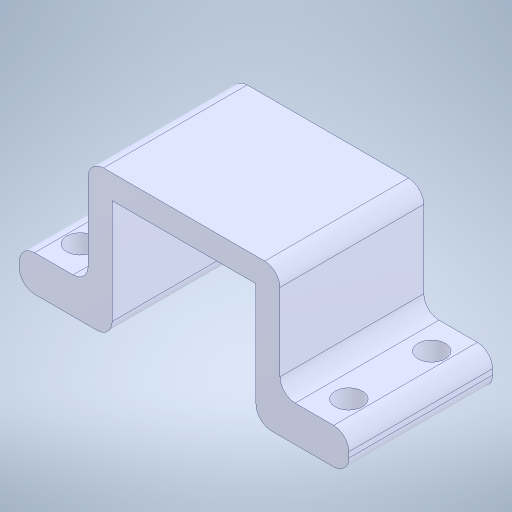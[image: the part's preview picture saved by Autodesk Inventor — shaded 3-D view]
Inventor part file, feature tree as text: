
AUTODESK INVENTOR PART (.ipt)
format: ipt  version: 2023.2 (Build 272271000, 271)  size: 238,080 bytes
history: mixed  units: in
note: dims shown in document units (in); Inventor stores cm internally (conversion verified against a paired STEP export)
features: fillet x1, imported_body x1
ambient origin geometry x8: Origin, YZ Plane, XZ Plane, XY Plane, X Axis, Y Axis, Z Axis, Center Point
bodies: Solid1 (imported_parasolid)
feature tree (2):
  fillet  "Fillet3"  [1 undecoded]
  imported_body  NMx_Import_Brep_tag  [imported B-rep: ~28 faces, bbox_mm=[27.5, 12.0, 12.0]]
note: 1 required parameter value undecoded (feature->parameter linkage not recoverable at this tier; creation-order binding heuristic only, values carry confidence <= 0.55)
